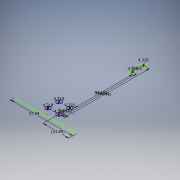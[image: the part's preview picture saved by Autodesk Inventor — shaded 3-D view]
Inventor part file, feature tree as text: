
AUTODESK INVENTOR PART (.ipt)
format: ipt  version: 2019 (Build 230136000, 136)  size: 100,864 bytes
history: native  units: in
note: dims shown in document units (in); Inventor stores cm internally (conversion verified against a paired STEP export)
features: sketch x1
ambient origin geometry x8: Origin, YZ Plane, XZ Plane, XY Plane, X Axis, Y Axis, Z Axis, Center Point
feature tree (1):
  sketch  "Sketch1"  dims[d0=0.17in d1=0.17in d3=0.23in d4=0.4in d5=0.17in d6=2.13in d7=2.7in d8=0.17in d9=0.23in d10=3.1in d12=2.2811in d13=0.17in d15=0.17in d16=0.9406in]
